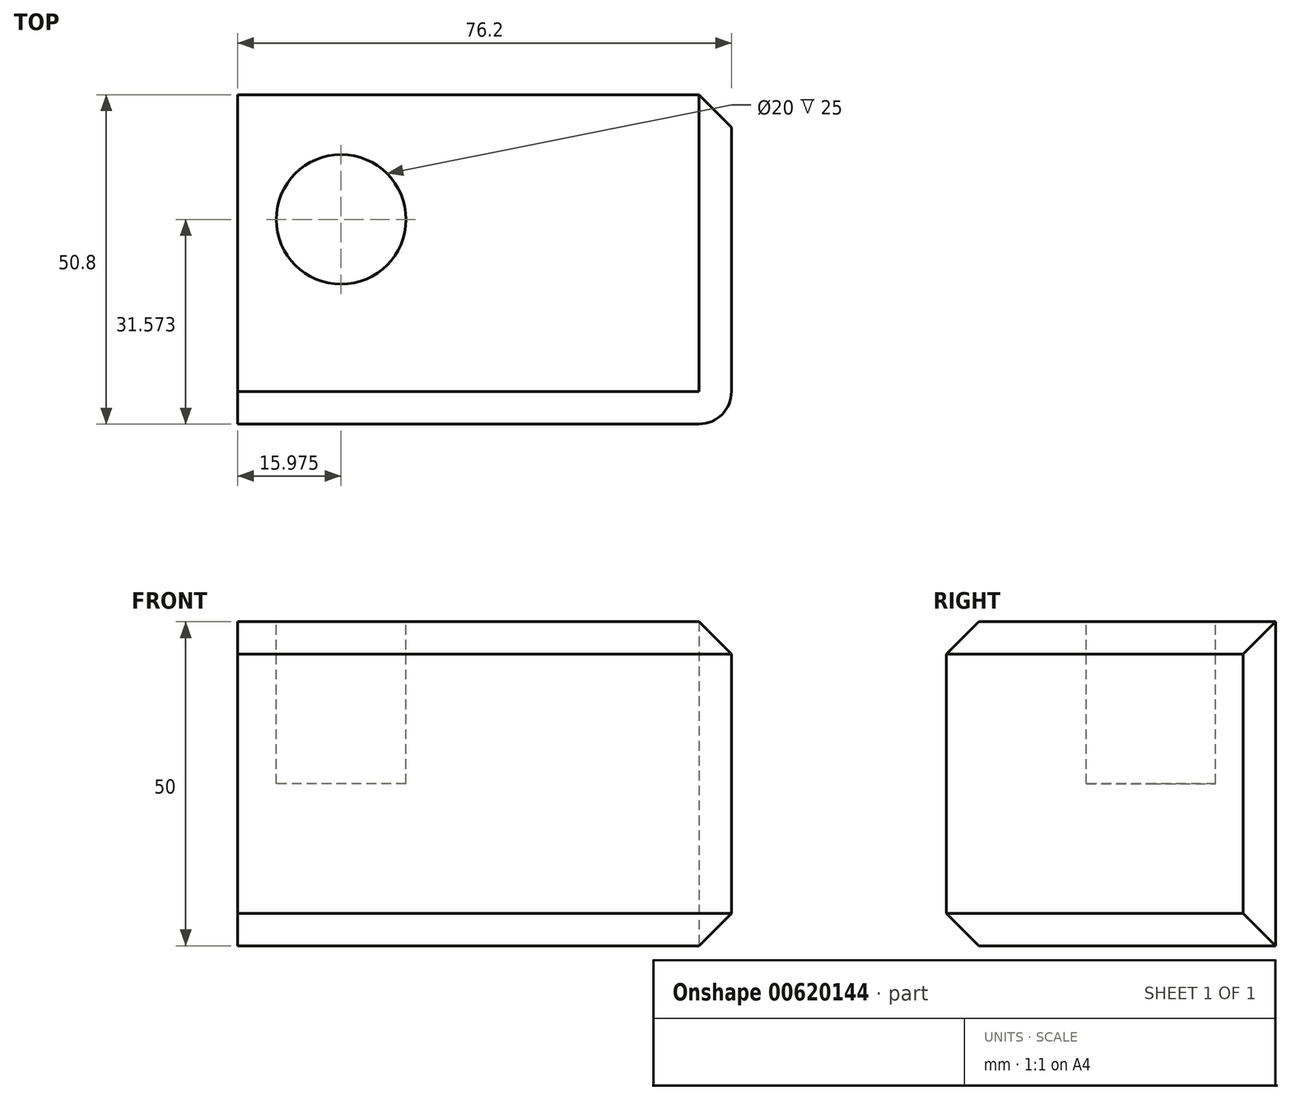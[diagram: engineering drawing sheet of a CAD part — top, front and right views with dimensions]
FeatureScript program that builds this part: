
annotation { "Feature Type Name" : "Feature", "Feature Type Description" : "" }
export const myFeature = defineFeature(function(context is Context, id is Id, definition is map)
    precondition{}
    {
        {
            var Q0;
            Q0=qCreatedBy(makeId("Top.planeOp"),FACE);
            var sketch = newSketch(context, id + "F0", { "sketchPlane" : qUnion([Q0])});
            skLineSegment(sketch, "E0.bottom", {"start": v(38.1, -25.4) * mm, "end": v(-38.1, -25.4) * mm});
            skLineSegment(sketch, "E0.top", {"start": v(38.1, 25.4) * mm, "end": v(-38.1, 25.4) * mm});
            skLineSegment(sketch, "E0.left", {"start": v(38.1, -25.4) * mm, "end": v(38.1, 25.4) * mm});
            skLineSegment(sketch, "E0.right", {"start": v(-38.1, -25.4) * mm, "end": v(-38.1, 25.4) * mm});
            skPoint(sketch, "E0.middle", {"position": v(0, 0) * mm});
            skSolve(sketch);
        }
        {
            var Q0;
            Q0 = qSketchRegion(id + "F0", true);
            extrude(context, id + "F1", {"entities" : qUnion([Q0]), "endBound" : BoundingType.SYMMETRIC, "depth" : 50 * mm, "offsetDistance" : 25 * mm});
        }
        {
            var Q0;
            Q0=makeQuery(id+"F1.opExtrude","CAP_FACE",FACE,{"disambiguationData":[OSD([sQuery(id+"F0.wireOp",EDGE,"E0.bottom"),sQuery(id+"F0.wireOp",EDGE,"E0.top"),sQuery(id+"F0.wireOp",EDGE,"E0.left"),sQuery(id+"F0.wireOp",EDGE,"E0.right")])],"isStart":false});
            var sketch = newSketch(context, id + "F2", { "sketchPlane" : qUnion([Q0])});
            skCircle(sketch, "E1", {"center": v(-22.12, 6.17) * mm, "radius": 10 * mm});
            skSolve(sketch);
        }
        {
            var Q0;
            Q0=makeQuery(id+"F2.imprint","IMPRINT",FACE,{"disambiguationData":[TD([[makeQuery(id+"F2.imprint","IMPRINT",EDGE,{"derivedFrom":sQuery(id+"F2.wireOp",EDGE,"E1")}),1.0]])]});
            extrude(context, id + "F3", {"entities" : qUnion([Q0]), "operationType" : NewBodyOperationType.REMOVE, "oppositeDirection" : true, "depth" : 25 * mm, "offsetDistance" : 25 * mm});
        }
        {
            var Q0;
            Q0=makeQuery(id+"F1.opExtrude","SWEPT_EDGE",EDGE,{"disambiguationData":[OSD([sQuery(id+"F0.wireOp",EDGE,"E0.bottom"),sQuery(id+"F0.wireOp",EDGE,"E0.left")])]});
            fillet(context, id + "F4", {"entities" : qUnion([Q0]), "radius" : 5 * mm, "tangentPropagation" : true, "allowEdgeOverflow" : false});
        }
        {
            var Q0;
            Q0=makeQuery(id+"F1.opExtrude","SWEPT_FACE",FACE,{"disambiguationData":[OSD([sQuery(id+"F0.wireOp",EDGE,"E0.left")])]});
            chamfer(context, id + "F5", {"entities" : qUnion([Q0]), "width" : 5 * mm, "tangentPropagation" : true});
        }
    });
